# Revit family: DuraCare-Dining_Chair-Conway+
name_source: partatom
category: Furniture
units: mm (PartAtom-declared; Revit-internal decimal feet)

## family parameters
Always vertical = Yes
Cut with Voids When Loaded = No
OmniClass Number = 23.40.20.00
OmniClass Title = General Furniture and Specialties
Room Calculation Point = No
Shared = No
Work Plane-Based = No

## types (2) — shared parameters
Arm Height = 26"
Assembly Code = E2020200
Back Contrasting Finish = DUR - Fabric 2
Boot Finish = DUR - Plastic Boot
Default Elevation = 0"
Depth = 23 1/2"
Height = 32"
Keynote = 12500
Low Emitting Finish = Yes
Low Emitting Material = Yes
Manufacturer = DuraCare Seating
Product Documentation Link = https://duracareseating.com
Revit Model Built By = https://servex-us.com
Salvage or Reuse = Yes
Seat Height = 18 3/4"
Type Comments = Conway
URL = https://duracareseating.com
Wheel Finish = DUR - Plastic Black
Width = 24"
zero-valued in all types: Percentage of Recycled Content

## per-type parameters (varying)
| type | Description | LD |
| AC-680 | Dining Chair 24"W x 23.5"D x 32"H - aluminum frame - wood grain finish | No |
| AC-680-LD | Dining Chair 22"W x 24"D x 32"H - aluminum frame - wood grain finish | Yes |

note: column(s) folded — value = type name in every type: Model

## geometry (parser evidence)
native form markers: Sweep x5
no freeform markers — native parametric forms only
